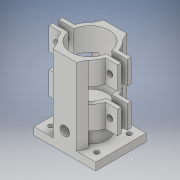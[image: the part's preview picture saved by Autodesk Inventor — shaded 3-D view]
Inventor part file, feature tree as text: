
AUTODESK INVENTOR PART (.ipt)
format: ipt  version: 2018 (Build 220112000, 112)  size: 296,448 bytes
history: native  units: in
note: dims shown in document units (in); Inventor stores cm internally (conversion verified against a paired STEP export)
features: extrude x6, sketch x6, plane x1, mirror x1
ambient origin geometry x8: Origin, YZ Plane, XZ Plane, XY Plane, X Axis, Y Axis, Z Axis, Center Point
bodies: Solid1 (feature_tree)
feature tree (14):
  extrude  "Extrusion1"  Depth=1.64in
  plane  "Work Plane1"
  extrude  "Extrusion3"  Depth=0.24in
  extrude  "Extrusion4"  Depth=0.257in
  extrude  "Extrusion5"  Depth=0.257in
  mirror  "Mirror1"
  extrude  "Extrusion6"  Depth=0.25in
  extrude  "Extrusion7"  Depth=0.25in
  sketch  "Sketch1"  dims[d0=0.1562in d1=1.64in]
  sketch  "Sketch3"  dims[d2=2.01in d3=0.24in]
  sketch  "Sketch6"  dims[d4=0.293in d5=0.257in]
  sketch  "Sketch7"  dims[d6=0.293in d7=0.257in]
  sketch  "Sketch8"  dims[d8=0.25in d9=0.0in d10=2.5in]
  sketch  "Sketch9"  dims[d20=0.125in d21=1.25in d22=0.125in d23=0.125in d24=0.1875in d25=0.0938in d26=0.625in d27=0.125in d28=0.125in d29=0.125in d30=0.0938in d31=0.0938in d32=0.75in d33=0.375in d34=1.0in d35=2.5in d36=0.0in d37=0.5in d38=0.5in d39=0.75in d40=2.5in d41=0.0in d43=0.5in d44=0.5in d45=0.25in d46=0.25in d47=0.25in d48=0.25in d49=2.5in d50=0.0in d51=0.1935in d52=1.13in d53=0.75in d54=0.0in d55=0.31in d57=0.381in d58=2.4375in d59=0.0in]
